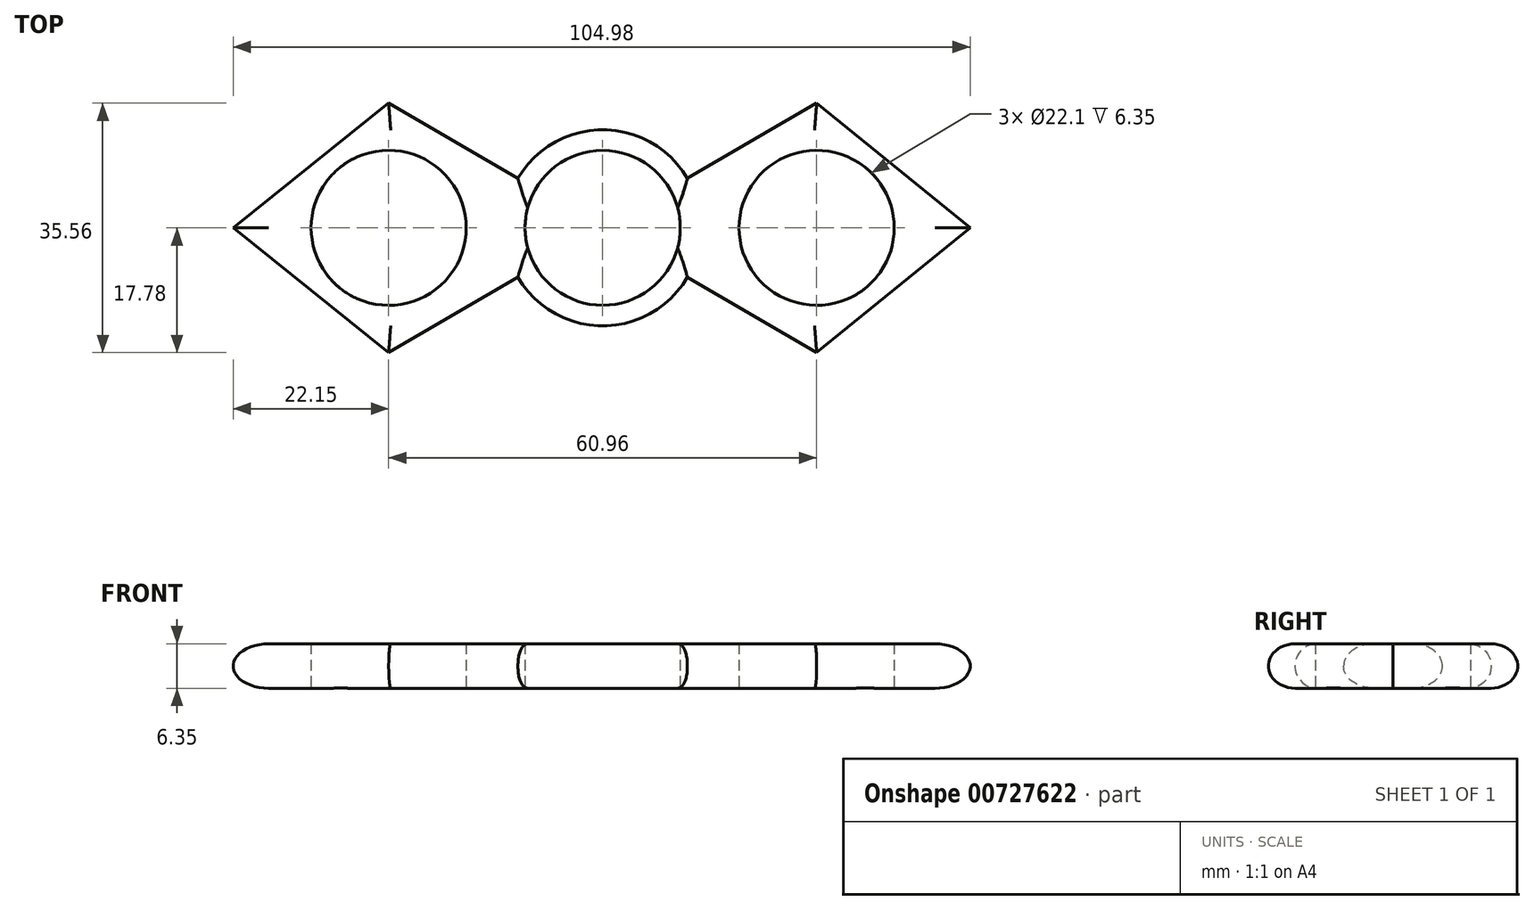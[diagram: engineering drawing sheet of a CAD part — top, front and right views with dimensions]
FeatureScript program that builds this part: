
annotation { "Feature Type Name" : "Feature", "Feature Type Description" : "" }
export const myFeature = defineFeature(function(context is Context, id is Id, definition is map)
    precondition{}
    {
        {
            var Q0;
            Q0=qCreatedBy(makeId("Top.planeOp"),FACE);
            var sketch = newSketch(context, id + "F0", { "sketchPlane" : qUnion([Q0])});
            skCircle(sketch, "E0", {"center": v(0, 0) * mm, "radius": 11.05 * mm});
            skCircle(sketch, "E1", {"center": v(0, 0) * mm, "radius": 13.97 * mm});
            skLineSegment(sketch, "E2", {"start": v(0, 0) * mm, "end": v(30.48, 0) * mm});
            skCircle(sketch, "E3", {"center": v(30.48, 0) * mm, "radius": 11.05 * mm});
            skLineSegment(sketch, "E4", {"start": v(0, 0) * mm, "end": v(-30.48, 0) * mm});
            skCircle(sketch, "E5", {"center": v(-30.48, 0) * mm, "radius": 11.05 * mm});
            skLineSegment(sketch, "E6", {"start": v(30.48, 0) * mm, "end": v(30.48, -17.78) * mm});
            skLineSegment(sketch, "E7", {"start": v(30.48, 0) * mm, "end": v(30.48, 17.78) * mm});
            skLineSegment(sketch, "E8", {"start": v(12.07, 7.04) * mm, "end": v(30.48, 17.78) * mm});
            skLineSegment(sketch, "E9", {"start": v(12.07, -7.04) * mm, "end": v(30.48, -17.78) * mm});
            skLineSegment(sketch, "E10", {"start": v(-30.48, 0) * mm, "end": v(-30.48, -17.78) * mm});
            skLineSegment(sketch, "E11", {"start": v(-30.48, 0) * mm, "end": v(-30.48, 17.78) * mm});
            skLineSegment(sketch, "E12", {"start": v(-30.48, 17.78) * mm, "end": v(-12.07, 7.04) * mm});
            skLineSegment(sketch, "E13", {"start": v(-30.48, -17.78) * mm, "end": v(-12.07, -7.04) * mm});
            skLineSegment(sketch, "E14", {"start": v(-30.48, 0) * mm, "end": v(-52.63, 0) * mm});
            skLineSegment(sketch, "E15", {"start": v(-30.48, 0) * mm, "end": v(-41.53, 0) * mm});
            skLineSegment(sketch, "E16", {"start": v(30.48, 0) * mm, "end": v(52.35, 0) * mm});
            skLineSegment(sketch, "E17", {"start": v(30.48, 17.78) * mm, "end": v(52.35, 0) * mm});
            skLineSegment(sketch, "E18", {"start": v(30.48, -17.78) * mm, "end": v(52.35, 0) * mm});
            skLineSegment(sketch, "E19", {"start": v(-52.63, 0) * mm, "end": v(-30.48, 17.78) * mm});
            skLineSegment(sketch, "E20", {"start": v(-52.63, 0) * mm, "end": v(-30.48, -17.78) * mm});
            skSolve(sketch);
        }
        {
            var Q0;
            Q0 = qSketchRegion(id + "F0", true);
            extrude(context, id + "F1", {"entities" : qUnion([Q0]), "depth" : 6.35 * mm, "offsetDistance" : 25.4 * mm});
        }
        {
            var Q0;
            Q0=makeQuery(id+"F1.opExtrude","CAP_EDGE",EDGE,{"disambiguationData":[OSD([sQuery(id+"F0.wireOp",EDGE,"E12")])],"isStart":false});
            var Q1;
            Q1=makeQuery(id+"F1.opExtrude","CAP_EDGE",EDGE,{"disambiguationData":[OSD([sQuery(id+"F0.wireOp",EDGE,"E19")])],"isStart":false});
            var Q2;
            Q2=makeQuery(id+"F1.opExtrude","CAP_EDGE",EDGE,{"disambiguationData":[OSD([sQuery(id+"F0.wireOp",EDGE,"E20")])],"isStart":false});
            var Q3;
            Q3=makeQuery(id+"F1.opExtrude","CAP_EDGE",EDGE,{"disambiguationData":[OSD([sQuery(id+"F0.wireOp",EDGE,"E13")])],"isStart":false});
            var Q4;
            {var subQ0=sQuery(id+"F0.wireOp",EDGE,"E1");Q4=makeQuery(id+"F1.opExtrude","CAP_EDGE",EDGE,{"disambiguationData":[OSD([subQ0]),TDD([makeQuery(id+"F0.imprint","IMPRINT",EDGE,{"disambiguationData":[TD([[makeQuery(id+"F0.imprint","INTERSECT",VERTEX,{"derivedFrom":[subQ0,sQuery(id+"F0.wireOp",EDGE,"E9")]}),1.0]])],"derivedFrom":subQ0})])],"isStart":false});}
            var Q5;
            Q5=makeQuery(id+"F1.opExtrude","CAP_EDGE",EDGE,{"disambiguationData":[OSD([sQuery(id+"F0.wireOp",EDGE,"E9")])],"isStart":false});
            var Q6;
            {var subQ0=sQuery(id+"F0.wireOp",EDGE,"E1");Q6=makeQuery(id+"F1.opExtrude","CAP_EDGE",EDGE,{"disambiguationData":[OSD([subQ0]),TDD([makeQuery(id+"F0.imprint","IMPRINT",EDGE,{"disambiguationData":[TD([[makeQuery(id+"F0.imprint","INTERSECT",VERTEX,{"derivedFrom":[subQ0,sQuery(id+"F0.wireOp",EDGE,"E8")]}),-1.0]])],"derivedFrom":subQ0})])],"isStart":false});}
            var Q7;
            Q7=makeQuery(id+"F1.opExtrude","CAP_EDGE",EDGE,{"disambiguationData":[OSD([sQuery(id+"F0.wireOp",EDGE,"E8")])],"isStart":false});
            var Q8;
            Q8=makeQuery(id+"F1.opExtrude","CAP_EDGE",EDGE,{"disambiguationData":[OSD([sQuery(id+"F0.wireOp",EDGE,"E17")])],"isStart":false});
            var Q9;
            Q9=makeQuery(id+"F1.opExtrude","CAP_EDGE",EDGE,{"disambiguationData":[OSD([sQuery(id+"F0.wireOp",EDGE,"E18")])],"isStart":false});
            var Q10;
            Q10=makeQuery(id+"F1.opExtrude","CAP_EDGE",EDGE,{"disambiguationData":[OSD([sQuery(id+"F0.wireOp",EDGE,"E17")])],"isStart":true});
            var Q11;
            Q11=makeQuery(id+"F1.opExtrude","CAP_EDGE",EDGE,{"disambiguationData":[OSD([sQuery(id+"F0.wireOp",EDGE,"E18")])],"isStart":true});
            var Q12;
            {var subQ0=sQuery(id+"F0.wireOp",EDGE,"E1");Q12=makeQuery(id+"F1.opExtrude","CAP_EDGE",EDGE,{"disambiguationData":[OSD([subQ0]),TDD([makeQuery(id+"F0.imprint","IMPRINT",EDGE,{"disambiguationData":[TD([[makeQuery(id+"F0.imprint","INTERSECT",VERTEX,{"derivedFrom":[subQ0,sQuery(id+"F0.wireOp",EDGE,"E8")]}),-1.0]])],"derivedFrom":subQ0})])],"isStart":true});}
            var Q13;
            Q13=makeQuery(id+"F1.opExtrude","CAP_EDGE",EDGE,{"disambiguationData":[OSD([sQuery(id+"F0.wireOp",EDGE,"E8")])],"isStart":true});
            var Q14;
            Q14=makeQuery(id+"F1.opExtrude","CAP_EDGE",EDGE,{"disambiguationData":[OSD([sQuery(id+"F0.wireOp",EDGE,"E9")])],"isStart":true});
            var Q15;
            {var subQ0=sQuery(id+"F0.wireOp",EDGE,"E1");Q15=makeQuery(id+"F1.opExtrude","CAP_EDGE",EDGE,{"disambiguationData":[OSD([subQ0]),TDD([makeQuery(id+"F0.imprint","IMPRINT",EDGE,{"disambiguationData":[TD([[makeQuery(id+"F0.imprint","INTERSECT",VERTEX,{"derivedFrom":[subQ0,sQuery(id+"F0.wireOp",EDGE,"E9")]}),1.0]])],"derivedFrom":subQ0})])],"isStart":true});}
            var Q16;
            Q16=makeQuery(id+"F1.opExtrude","CAP_EDGE",EDGE,{"disambiguationData":[OSD([sQuery(id+"F0.wireOp",EDGE,"E13")])],"isStart":true});
            var Q17;
            Q17=makeQuery(id+"F1.opExtrude","CAP_EDGE",EDGE,{"disambiguationData":[OSD([sQuery(id+"F0.wireOp",EDGE,"E12")])],"isStart":true});
            var Q18;
            Q18=makeQuery(id+"F1.opExtrude","CAP_EDGE",EDGE,{"disambiguationData":[OSD([sQuery(id+"F0.wireOp",EDGE,"E20")])],"isStart":true});
            var Q19;
            Q19=makeQuery(id+"F1.opExtrude","CAP_EDGE",EDGE,{"disambiguationData":[OSD([sQuery(id+"F0.wireOp",EDGE,"E19")])],"isStart":true});
            fillet(context, id + "F2", {"entities" : qUnion([Q0, Q1, Q2, Q3, Q4, Q5, Q6, Q7, Q8, Q9, Q10, Q11, Q12, Q13, Q14, Q15, Q16, Q17, Q18, Q19]), "radius" : 3.17 * mm, "tangentPropagation" : true, "allowEdgeOverflow" : false});
        }
    });
